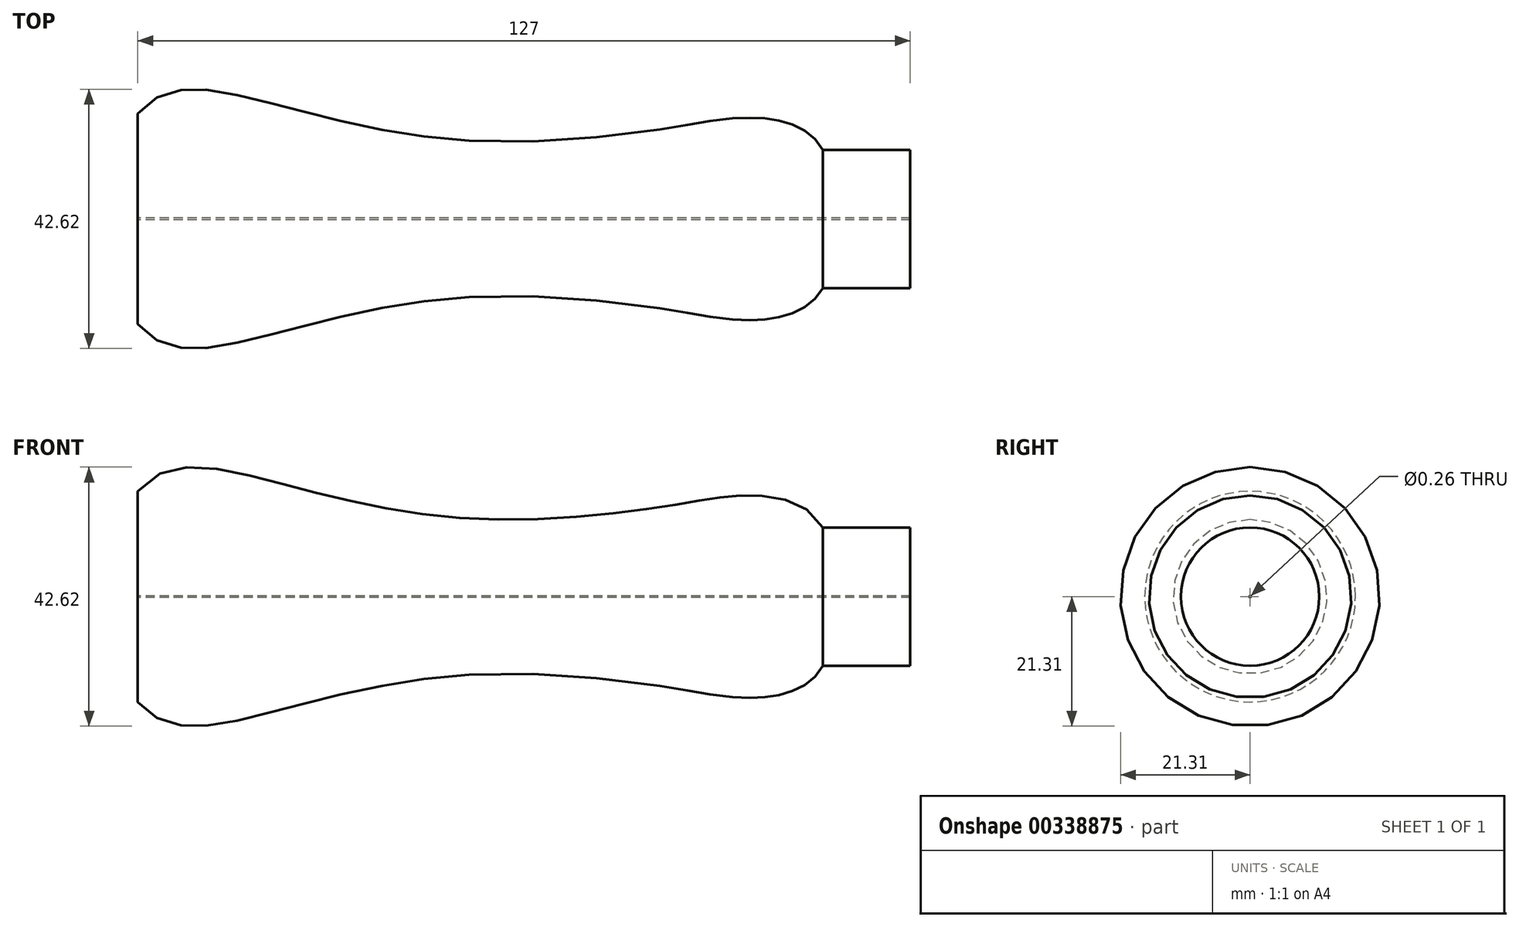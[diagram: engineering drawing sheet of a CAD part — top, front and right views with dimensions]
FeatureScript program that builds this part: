
annotation { "Feature Type Name" : "Feature", "Feature Type Description" : "" }
export const myFeature = defineFeature(function(context is Context, id is Id, definition is map)
    precondition{}
    {
        {
            var Q0;
            Q0=qCreatedBy(makeId("Front.planeOp"),FACE);
            var sketch = newSketch(context, id + "F0", { "sketchPlane" : qUnion([Q0])});
            skFitSpline(sketch, "E0", {"points": [v(-67.56, 0) * mm, v(-46.32, -1.86) * mm, v(-13.02, 4.5) * mm, v(20.66, 2.25) * mm, v(32.99, 0.68) * mm, v(45.1, 5.95) * mm], "startDerivative": vector(74, -91.46) * mm, "endDerivative": vector(49.3, 85.95) * mm});
            skLineSegment(sketch, "E1", {"start": v(45.1, 5.95) * mm, "end": v(59.44, 5.95) * mm});
            skLineSegment(sketch, "E2", {"start": v(-68.64, 17.32) * mm, "end": v(72.03, 17.32) * mm, "construction": true});
            skFitSpline(sketch, "E3", {"points": [v(-67.56, 0) * mm, v(-67.56, 17.2) * mm], "startDerivative": vector(0, 17.2) * mm, "endDerivative": vector(0, 17.2) * mm});
            skLineSegment(sketch, "E4", {"start": v(59.44, 5.95) * mm, "end": v(59.44, 17.2) * mm});
            skLineSegment(sketch, "E5", {"start": v(59.44, 17.2) * mm, "end": v(-67.56, 17.2) * mm});
            skSolve(sketch);
        }
        {
            var Q0;
            Q0=makeQuery(id+"F0.imprint","IMPRINT",FACE,{"disambiguationData":[TD([[makeQuery(id+"F0.imprint","IMPRINT",EDGE,{"derivedFrom":sQuery(id+"F0.wireOp",EDGE,"E0")}),1.0]])]});
            var Q1;
            Q1=sQuery(id+"F0.wireOp",EDGE,"E2");
            revolve(context, id + "F1", {"entities" : qUnion([Q0]), "axis" : qUnion([Q1]), "revolveType" : RevolveType.FULL});
        }
    });
